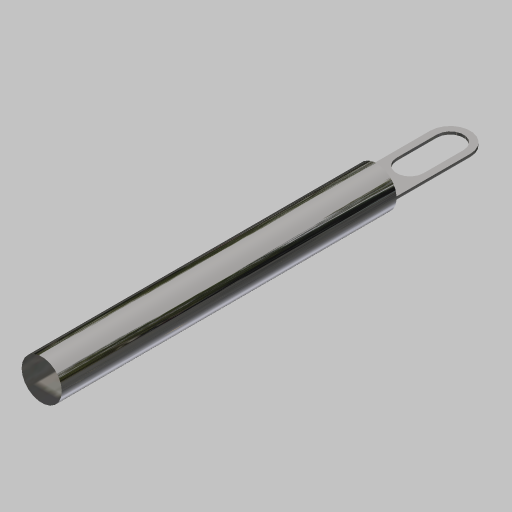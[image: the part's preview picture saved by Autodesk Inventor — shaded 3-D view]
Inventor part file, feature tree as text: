
AUTODESK INVENTOR PART (.ipt)
format: ipt  version: 2023 (Build 270158000, 158)  size: 172,032 bytes
history: native  units: mm
features: extrude x3, sketch x3, fillet x1, projected_geometry x1
ambient origin geometry x8: Origin, YZ Plane, XZ Plane, XY Plane, X Axis, Y Axis, Z Axis, Center Point
bodies: Volumenkörper1 (feature_tree)
feature tree (8):
  extrude  "Extrusion1"  Depth=32.0mm TaperAngle=0.0deg
  extrude  "Extrusion2"  Depth=1.4mm
  fillet  "Rundung1"  Radius=7.0mm
  extrude  "Extrusion3"  Depth=2.0mm
  sketch  "Skizze1"  dims[d0=3.0mm d1=32.0mm d2=0.0mm]
  sketch  "Skizze2"  dims[d3=7.0mm d4=1.4mm d5=7.0mm]
  sketch  "Skizze3"  dims[d6=0.2mm d7=7.0mm d8=1.4mm d9=8.0mm d10=3.0mm d11=35.0mm d12=0.0mm d13=1.5mm d14=3.0mm d15=2.0mm d16=35.0mm d17=0.0mm d18=7.0mm]
  projected_geometry  "Projizierte Kontur1"
